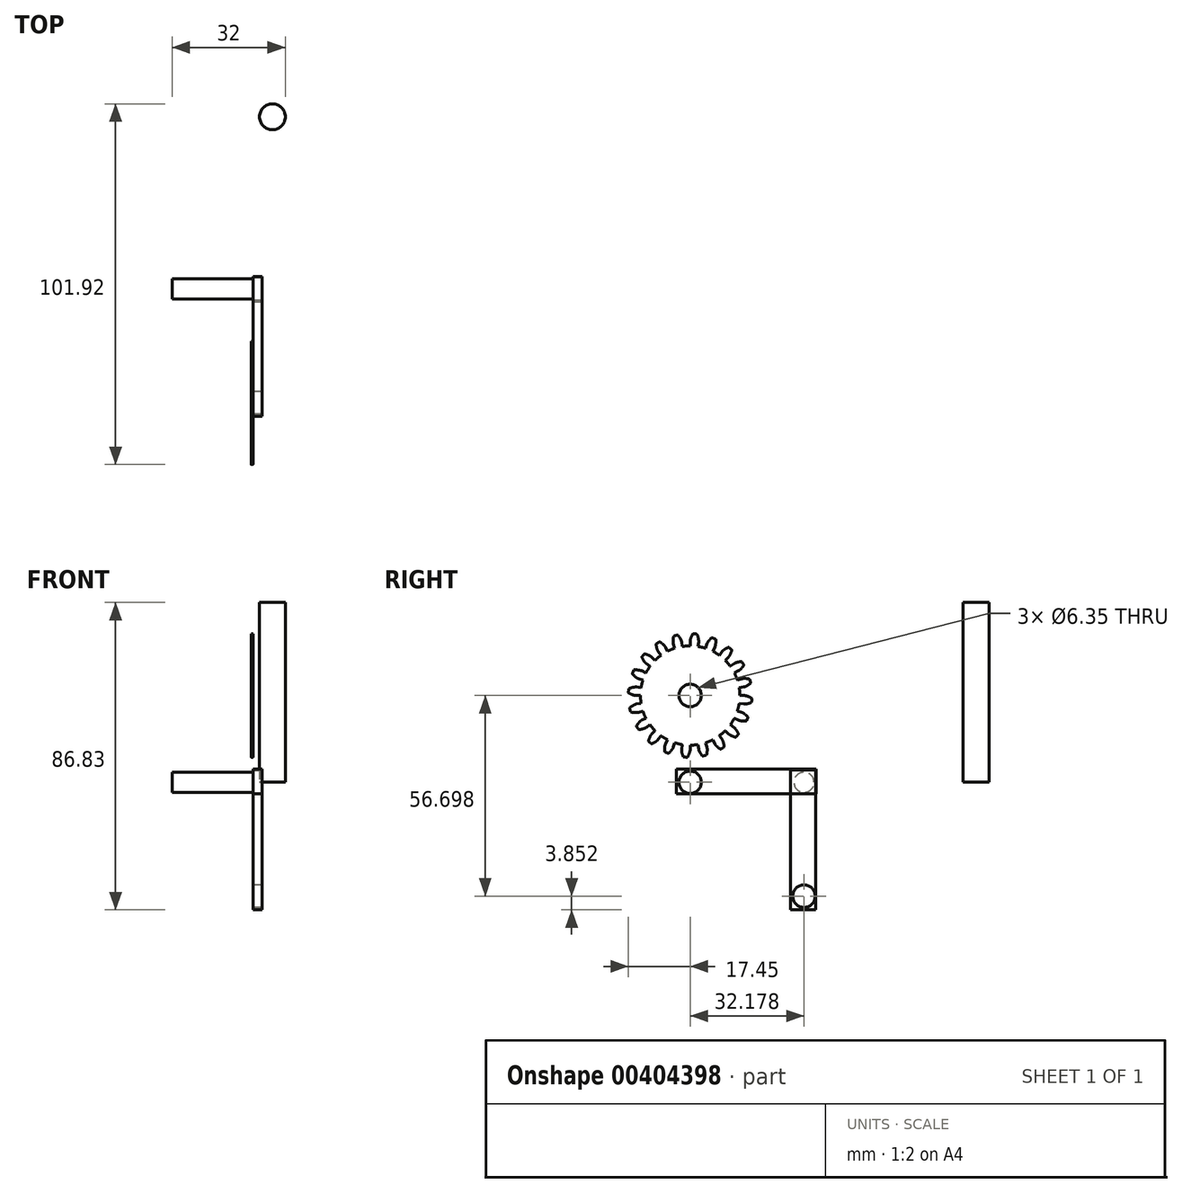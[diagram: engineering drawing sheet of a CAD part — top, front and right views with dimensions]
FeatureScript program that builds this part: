
annotation { "Feature Type Name" : "Feature", "Feature Type Description" : "" }
export const myFeature = defineFeature(function(context is Context, id is Id, definition is map)
    precondition{}
    {
        {
            assignVariable(context, id + "F0", {"name" : "NumberTeeth", "anyValue" : 20});
        }
        {
            assignVariable(context, id + "F1", {"name" : "GearThickness", "anyValue" : .5});
        }
        {
            var Q0;
            Q0=qCreatedBy(makeId("Right.planeOp"),FACE);
            var sketch = newSketch(context, id + "F2", { "sketchPlane" : qUnion([Q0])});
            skCircle(sketch, "E0", {"center": v(0, 0) * mm, "radius": 14.04 * mm});
            skCircle(sketch, "E1", {"center": v(0, 0) * mm, "radius": 15.37 * mm, "construction": true});
            skCircle(sketch, "E2", {"center": v(0, 0) * mm, "radius": 15.88 * mm, "construction": true});
            skCircle(sketch, "E3", {"center": v(0, 0) * mm, "radius": 17.46 * mm});
            skLineSegment(sketch, "E4", {"start": v(0, 0) * mm, "end": v(-15.37, 0) * mm, "construction": true});
            skLineSegment(sketch, "E5.1.0", {"start": v(0, 0) * mm, "end": v(-15.35, 0.77) * mm, "construction": true});
            skLineSegment(sketch, "E5.2.0", {"start": v(0, 0) * mm, "end": v(-15.3, 1.53) * mm, "construction": true});
            skLineSegment(sketch, "E5.3.0", {"start": v(0, 0) * mm, "end": v(-15.2, 2.3) * mm, "construction": true});
            skLineSegment(sketch, "E5.4.0", {"start": v(0, 0) * mm, "end": v(-15.06, 3.05) * mm, "construction": true});
            skLineSegment(sketch, "E5.5.0", {"start": v(0, 0) * mm, "end": v(-14.9, 3.8) * mm, "construction": true});
            skLineSegment(sketch, "E5.6.0", {"start": v(0, 0) * mm, "end": v(-14.68, 4.54) * mm, "construction": true});
            skLineSegment(sketch, "E5.7.0", {"start": v(0, 0) * mm, "end": v(-14.44, 5.27) * mm, "construction": true});
            skLineSegment(sketch, "E5.8.0", {"start": v(0, 0) * mm, "end": v(-14.16, 5.99) * mm, "construction": true});
            skLineSegment(sketch, "E5.9.0", {"start": v(0, 0) * mm, "end": v(-13.84, 6.69) * mm, "construction": true});
            skLineSegment(sketch, "E5.10.0", {"start": v(0, 0) * mm, "end": v(-13.49, 7.37) * mm, "construction": true});
            skLineSegment(sketch, "E5.11.0", {"start": v(0, 0) * mm, "end": v(-13.1, 8.03) * mm, "construction": true});
            skLineSegment(sketch, "E5.12.0", {"start": v(0, 0) * mm, "end": v(-12.68, 8.68) * mm, "construction": true});
            skLineSegment(sketch, "E5.13.0", {"start": v(0, 0) * mm, "end": v(-12.24, 9.3) * mm, "construction": true});
            skLineSegment(sketch, "E5.14.0", {"start": v(0, 0) * mm, "end": v(-11.76, 9.9) * mm, "construction": true});
            skLineSegment(sketch, "E5.anchor2", {"start": v(0, 0) * mm, "end": v(-11.76, 9.9) * mm, "construction": true});
            skLineSegment(sketch, "E6", {"start": v(-15.35, 0.77) * mm, "end": v(-15.39, 0) * mm, "construction": true});
            skLineSegment(sketch, "E7", {"start": v(-15.3, 1.53) * mm, "end": v(-15.45, 0) * mm, "construction": true});
            skLineSegment(sketch, "E8", {"start": v(-15.2, 2.3) * mm, "end": v(-15.54, 0.02) * mm, "construction": true});
            skLineSegment(sketch, "E9", {"start": v(-14.9, 3.8) * mm, "end": v(-15.84, 0.08) * mm, "construction": true});
            skLineSegment(sketch, "E10", {"start": v(-14.68, 4.54) * mm, "end": v(-16.05, 0.14) * mm, "construction": true});
            skLineSegment(sketch, "E11", {"start": v(-14.44, 5.27) * mm, "end": v(-16.28, 0.22) * mm, "construction": true});
            skLineSegment(sketch, "E12", {"start": v(-14.16, 5.99) * mm, "end": v(-16.55, 0.32) * mm, "construction": true});
            skLineSegment(sketch, "E13", {"start": v(-13.84, 6.69) * mm, "end": v(-16.85, 0.46) * mm, "construction": true});
            skLineSegment(sketch, "E14", {"start": v(-13.49, 7.37) * mm, "end": v(-17.17, 0.62) * mm, "construction": true});
            skLineSegment(sketch, "E15", {"start": v(-13.1, 8.03) * mm, "end": v(-17.52, 0.83) * mm, "construction": true});
            skLineSegment(sketch, "E16", {"start": v(-15.06, 3.05) * mm, "end": v(-15.67, 0.04) * mm, "construction": true});
            skLineSegment(sketch, "E17", {"start": v(-12.68, 8.68) * mm, "end": v(-17.9, 1.07) * mm, "construction": true});
            skLineSegment(sketch, "E18", {"start": v(-12.24, 9.3) * mm, "end": v(-18.28, 1.35) * mm, "construction": true});
            skLineSegment(sketch, "E19", {"start": v(-11.76, 9.9) * mm, "end": v(-18.69, 1.67) * mm, "construction": true});
            skLineSegment(sketch, "E20", {"start": v(0, 0) * mm, "end": v(-15.32, 1.2) * mm, "construction": true});
            skLineSegment(sketch, "E21", {"start": v(-14.04, 0) * mm, "end": v(-15.37, 0) * mm});
            skLineSegment(sketch, "E22.MirrorCS", {"start": v(-13.87, 2.2) * mm, "end": v(-15.18, 2.4) * mm});
            skFitSpline(sketch, "E23", {"points": [v(-15.37, 0) * mm, v(-15.39, 0) * mm, v(-15.45, 0) * mm, v(-15.54, 0.02) * mm, v(-15.67, 0.04) * mm, v(-15.84, 0.08) * mm, v(-16.05, 0.14) * mm, v(-16.28, 0.22) * mm, v(-16.55, 0.32) * mm, v(-16.85, 0.46) * mm, v(-17.17, 0.62) * mm, v(-17.52, 0.83) * mm, v(-17.9, 1.07) * mm, v(-18.28, 1.35) * mm, v(-18.69, 1.67) * mm], "startDerivative": vector(-0.82, 0) * mm, "endDerivative": vector(-1.2, 1) * mm});
            skLineSegment(sketch, "E24", {"start": v(-18.69, 1.67) * mm, "end": v(-19.04, 1.97) * mm, "construction": true});
            skFitSpline(sketch, "E25.MirrorCS", {"points": [v(-15.18, 2.4) * mm, v(-15.2, 2.4) * mm, v(-15.26, 2.41) * mm, v(-15.35, 2.41) * mm, v(-15.49, 2.41) * mm, v(-15.66, 2.4) * mm, v(-15.87, 2.37) * mm, v(-16.12, 2.33) * mm, v(-16.4, 2.27) * mm, v(-16.71, 2.18) * mm, v(-17.06, 2.07) * mm, v(-17.43, 1.92) * mm, v(-17.84, 1.74) * mm, v(-18.27, 1.53) * mm, v(-18.72, 1.27) * mm], "startDerivative": vector(-0.8, 0.13) * mm, "endDerivative": vector(-1.34, -0.8) * mm});
            skSolve(sketch);
        }
        {
            var Q0;
            {var subQ0=sQuery(id+"F2.wireOp",EDGE,"E0");var subQ27=makeQuery(id+"F2.imprint","INTERSECT",VERTEX,{"derivedFrom":[subQ0,sQuery(id+"F2.wireOp",EDGE,"10ea1024-8cf5-41f5-a75f-a634b86921f3.10.0")]});Q0=makeQuery(id+"F2.imprint","IMPRINT",FACE,{"disambiguationData":[TD([[makeQuery(id+"F2.imprint","IMPRINT",EDGE,{"disambiguationData":[TD([[subQ27,-1.0]])],"derivedFrom":subQ0}),1.0]])]});}
            var Q1;
            {var subQ0=sQuery(id+"F2.wireOp",EDGE,"10ea1024-8cf5-41f5-a75f-a634b86921f3.1.0");Q1=makeQuery(id+"F2.imprint","IMPRINT",FACE,{"disambiguationData":[TD([[makeQuery(id+"F2.imprint","IMPRINT",EDGE,{"derivedFrom":subQ0}),-1.0]])]});}
            var Q2;
            {var subQ7=sQuery(id+"F2.wireOp",EDGE,"10ea1024-8cf5-41f5-a75f-a634b86921f3.2.0");Q2=makeQuery(id+"F2.imprint","IMPRINT",FACE,{"disambiguationData":[TD([[makeQuery(id+"F2.imprint","IMPRINT",EDGE,{"derivedFrom":subQ7}),-1.0]])]});}
            var Q3;
            {var subQ8=sQuery(id+"F2.wireOp",EDGE,"10ea1024-8cf5-41f5-a75f-a634b86921f3.3.0");Q3=makeQuery(id+"F2.imprint","IMPRINT",FACE,{"disambiguationData":[TD([[makeQuery(id+"F2.imprint","IMPRINT",EDGE,{"derivedFrom":subQ8}),-1.0]])]});}
            var Q4;
            {var subQ2=sQuery(id+"F2.wireOp",EDGE,"10ea1024-8cf5-41f5-a75f-a634b86921f3.4.0");Q4=makeQuery(id+"F2.imprint","IMPRINT",FACE,{"disambiguationData":[TD([[makeQuery(id+"F2.imprint","IMPRINT",EDGE,{"derivedFrom":subQ2}),-1.0]])]});}
            var Q5;
            {var subQ8=sQuery(id+"F2.wireOp",EDGE,"10ea1024-8cf5-41f5-a75f-a634b86921f3.5.0");Q5=makeQuery(id+"F2.imprint","IMPRINT",FACE,{"disambiguationData":[TD([[makeQuery(id+"F2.imprint","IMPRINT",EDGE,{"derivedFrom":subQ8}),-1.0]])]});}
            var Q6;
            {var subQ3=sQuery(id+"F2.wireOp",EDGE,"10ea1024-8cf5-41f5-a75f-a634b86921f3.6.0");Q6=makeQuery(id+"F2.imprint","IMPRINT",FACE,{"disambiguationData":[TD([[makeQuery(id+"F2.imprint","IMPRINT",EDGE,{"derivedFrom":subQ3}),-1.0]])]});}
            var Q7;
            {var subQ0=sQuery(id+"F2.wireOp",EDGE,"10ea1024-8cf5-41f5-a75f-a634b86921f3.7.0");Q7=makeQuery(id+"F2.imprint","IMPRINT",FACE,{"disambiguationData":[TD([[makeQuery(id+"F2.imprint","IMPRINT",EDGE,{"derivedFrom":subQ0}),-1.0]])]});}
            var Q8;
            {var subQ5=sQuery(id+"F2.wireOp",EDGE,"10ea1024-8cf5-41f5-a75f-a634b86921f3.8.0");Q8=makeQuery(id+"F2.imprint","IMPRINT",FACE,{"disambiguationData":[TD([[makeQuery(id+"F2.imprint","IMPRINT",EDGE,{"derivedFrom":subQ5}),-1.0]])]});}
            var Q9;
            {var subQ1=sQuery(id+"F2.wireOp",EDGE,"10ea1024-8cf5-41f5-a75f-a634b86921f3.9.0");Q9=makeQuery(id+"F2.imprint","IMPRINT",FACE,{"disambiguationData":[TD([[makeQuery(id+"F2.imprint","IMPRINT",EDGE,{"derivedFrom":subQ1}),-1.0]])]});}
            var Q10;
            {var subQ5=sQuery(id+"F2.wireOp",EDGE,"10ea1024-8cf5-41f5-a75f-a634b86921f3.10.0");Q10=makeQuery(id+"F2.imprint","IMPRINT",FACE,{"disambiguationData":[TD([[makeQuery(id+"F2.imprint","IMPRINT",EDGE,{"derivedFrom":subQ5}),-1.0]])]});}
            var Q11;
            {var subQ8=sQuery(id+"F2.wireOp",EDGE,"10ea1024-8cf5-41f5-a75f-a634b86921f3.11.0");Q11=makeQuery(id+"F2.imprint","IMPRINT",FACE,{"disambiguationData":[TD([[makeQuery(id+"F2.imprint","IMPRINT",EDGE,{"derivedFrom":subQ8}),-1.0]])]});}
            var Q12;
            {var subQ2=sQuery(id+"F2.wireOp",EDGE,"10ea1024-8cf5-41f5-a75f-a634b86921f3.12.0");Q12=makeQuery(id+"F2.imprint","IMPRINT",FACE,{"disambiguationData":[TD([[makeQuery(id+"F2.imprint","IMPRINT",EDGE,{"derivedFrom":subQ2}),-1.0]])]});}
            var Q13;
            {var subQ3=sQuery(id+"F2.wireOp",EDGE,"10ea1024-8cf5-41f5-a75f-a634b86921f3.13.0");Q13=makeQuery(id+"F2.imprint","IMPRINT",FACE,{"disambiguationData":[TD([[makeQuery(id+"F2.imprint","IMPRINT",EDGE,{"derivedFrom":subQ3}),-1.0]])]});}
            var Q14;
            {var subQ0=sQuery(id+"F2.wireOp",EDGE,"10ea1024-8cf5-41f5-a75f-a634b86921f3.14.0");Q14=makeQuery(id+"F2.imprint","IMPRINT",FACE,{"disambiguationData":[TD([[makeQuery(id+"F2.imprint","IMPRINT",EDGE,{"derivedFrom":subQ0}),-1.0]])]});}
            var Q15;
            {var subQ6=sQuery(id+"F2.wireOp",EDGE,"10ea1024-8cf5-41f5-a75f-a634b86921f3.15.0");Q15=makeQuery(id+"F2.imprint","IMPRINT",FACE,{"disambiguationData":[TD([[makeQuery(id+"F2.imprint","IMPRINT",EDGE,{"derivedFrom":subQ6}),-1.0]])]});}
            var Q16;
            {var subQ5=sQuery(id+"F2.wireOp",EDGE,"10ea1024-8cf5-41f5-a75f-a634b86921f3.16.0");Q16=makeQuery(id+"F2.imprint","IMPRINT",FACE,{"disambiguationData":[TD([[makeQuery(id+"F2.imprint","IMPRINT",EDGE,{"derivedFrom":subQ5}),-1.0]])]});}
            var Q17;
            {var subQ7=sQuery(id+"F2.wireOp",EDGE,"10ea1024-8cf5-41f5-a75f-a634b86921f3.17.0");Q17=makeQuery(id+"F2.imprint","IMPRINT",FACE,{"disambiguationData":[TD([[makeQuery(id+"F2.imprint","IMPRINT",EDGE,{"derivedFrom":subQ7}),-1.0]])]});}
            var Q18;
            {var subQ5=sQuery(id+"F2.wireOp",EDGE,"10ea1024-8cf5-41f5-a75f-a634b86921f3.18.0");Q18=makeQuery(id+"F2.imprint","IMPRINT",FACE,{"disambiguationData":[TD([[makeQuery(id+"F2.imprint","IMPRINT",EDGE,{"derivedFrom":subQ5}),-1.0]])]});}
            var Q19;
            {var subQ8=sQuery(id+"F2.wireOp",EDGE,"10ea1024-8cf5-41f5-a75f-a634b86921f3.19.0");Q19=makeQuery(id+"F2.imprint","IMPRINT",FACE,{"disambiguationData":[TD([[makeQuery(id+"F2.imprint","IMPRINT",EDGE,{"derivedFrom":subQ8}),-1.0]])]});}
            var Q20;
            {var subQ8=sQuery(id+"F2.wireOp",EDGE,"E21");Q20=makeQuery(id+"F2.imprint","IMPRINT",FACE,{"disambiguationData":[TD([[makeQuery(id+"F2.imprint","IMPRINT",EDGE,{"derivedFrom":subQ8}),-1.0]])]});}
            extrude(context, id + "F3", {"entities" : qUnion([Q0, Q1, Q2, Q3, Q4, Q5, Q6, Q7, Q8, Q9, Q10, Q11, Q12, Q13, Q14, Q15, Q16, Q17, Q18, Q19, Q20]), "depth" : (getVariable(context, 'GearThickness')) * mm});
        }
        {
            var Q0;
            Q0=makeQuery(id+"F3.opExtrude","SWEPT_FACE",FACE,{"disambiguationData":[OSD([sQuery(id+"F2.wireOp",EDGE,"E25.MirrorCS")])]});
            var Q1;
            Q1=makeQuery(id+"F3.opExtrude","SWEPT_FACE",FACE,{"disambiguationData":[OSD([sQuery(id+"F2.wireOp",EDGE,"E23")])]});
            var Q2;
            Q2=makeQuery(id+"F3.opExtrude","SWEPT_FACE",FACE,{"disambiguationData":[OSD([sQuery(id+"F2.wireOp",EDGE,"E3")])]});
            var Q3;
            Q3=makeQuery(id+"F3.opExtrude","SWEPT_FACE",FACE,{"disambiguationData":[OSD([sQuery(id+"F2.wireOp",EDGE,"E22.MirrorCS")])]});
            var Q4;
            Q4=makeQuery(id+"F3.opExtrude","SWEPT_FACE",FACE,{"disambiguationData":[OSD([sQuery(id+"F2.wireOp",EDGE,"E21")])]});
            var Q5;
            Q5=makeQuery(id+"F3.opExtrude","SWEPT_FACE",FACE,{"disambiguationData":[OSD([sQuery(id+"F2.wireOp",EDGE,"E0")])]});
            circularPattern(context, id + "F4", {"faces" : qUnion([Q0, Q1, Q2, Q3, Q4]), "axis" : qUnion([Q5]), "angle" : 360 * degree, "instanceCount" : getVariable(context, 'NumberTeeth'), "equalSpace" : true, "patternType" : PatternType.FACE});
        }
        {
            var Q0;
            Q0=makeQuery(id+"F3.opExtrude","SWEPT_BODY",BODY,{"disambiguationData":[OSD([sQuery(id+"F2.wireOp",EDGE,"E0"),sQuery(id+"F2.wireOp",EDGE,"E3"),sQuery(id+"F2.wireOp",EDGE,"E21"),sQuery(id+"F2.wireOp",EDGE,"E22.MirrorCS"),sQuery(id+"F2.wireOp",EDGE,"E23"),sQuery(id+"F2.wireOp",EDGE,"E25.MirrorCS")])]});
            transform(context, id + "F5", {"entities" : qUnion([Q0]), "transformType" : TransformType.TRANSLATION_3D, "dx" : 0 * mm, "dy" : 33.33 * mm, "dz" : 0 * mm, "makeCopy" : true});
        }
        {
            var Q0;
            Q0=makeQuery(id+"F5.opPattern","COPY",BODY,{"derivedFrom":makeQuery(id+"F3.opExtrude","SWEPT_BODY",BODY,{"disambiguationData":[OSD([sQuery(id+"F2.wireOp",EDGE,"E0"),sQuery(id+"F2.wireOp",EDGE,"E3"),sQuery(id+"F2.wireOp",EDGE,"E21"),sQuery(id+"F2.wireOp",EDGE,"E22.MirrorCS"),sQuery(id+"F2.wireOp",EDGE,"E23"),sQuery(id+"F2.wireOp",EDGE,"E25.MirrorCS")])]}),"instanceName":"1"});
            transform(context, id + "F6", {"entities" : qUnion([Q0]), "transformType" : TransformType.TRANSLATION_3D, "dx" : 0 * mm, "dy" : -1.59 * mm, "dz" : 0 * mm, "makeCopy" : false});
        }
        {
            var Q0;
            Q0=makeQuery(id+"F3.opExtrude","CAP_FACE",FACE,{"disambiguationData":[OSD([sQuery(id+"F2.wireOp",EDGE,"E0"),sQuery(id+"F2.wireOp",EDGE,"E3"),sQuery(id+"F2.wireOp",EDGE,"E21"),sQuery(id+"F2.wireOp",EDGE,"E22.MirrorCS"),sQuery(id+"F2.wireOp",EDGE,"E23"),sQuery(id+"F2.wireOp",EDGE,"E25.MirrorCS")])],"isStart":false});
            var sketch = newSketch(context, id + "F7", { "sketchPlane" : qUnion([Q0])});
            skPoint(sketch, "E26", {"position": v(0, 0) * mm});
            skPoint(sketch, "E27", {"position": v(32.12, 0) * mm});
            skSolve(sketch);
        }
        {
            var Q0;
            Q0=sQuery(id+"F7.wireOp",VERTEX,"E26");
            var Q1;
            Q1=sQuery(id+"F7.wireOp",VERTEX,"E27");
            var Q2;
            Q2=makeQuery(id+"F3.opExtrude","SWEPT_BODY",BODY,{"disambiguationData":[OSD([sQuery(id+"F2.wireOp",EDGE,"E0"),sQuery(id+"F2.wireOp",EDGE,"E3"),sQuery(id+"F2.wireOp",EDGE,"E21"),sQuery(id+"F2.wireOp",EDGE,"E22.MirrorCS"),sQuery(id+"F2.wireOp",EDGE,"E23"),sQuery(id+"F2.wireOp",EDGE,"E25.MirrorCS")])]});
            var Q3;
            Q3=makeQuery(id+"F5.opPattern","COPY",BODY,{"derivedFrom":makeQuery(id+"F3.opExtrude","SWEPT_BODY",BODY,{"disambiguationData":[OSD([sQuery(id+"F2.wireOp",EDGE,"E0"),sQuery(id+"F2.wireOp",EDGE,"E3"),sQuery(id+"F2.wireOp",EDGE,"E21"),sQuery(id+"F2.wireOp",EDGE,"E22.MirrorCS"),sQuery(id+"F2.wireOp",EDGE,"E23"),sQuery(id+"F2.wireOp",EDGE,"E25.MirrorCS")])]}),"instanceName":"1"});
            hole(context, id + "F8", {"style" : HoleStyle.SIMPLE, "endStyle" : HoleEndStyle.THROUGH, "holeDiameter" : 6.35 * mm, "majorDiameter" : 6.35 * mm, "isTappedThrough" : true, "tappedDepth" : 12.7 * mm, "tapClearance" : 3, "locations" : qUnion([Q0, Q1]), "scope" : qUnion([Q2, Q3])});
        }
        {
            var Q0;
            Q0=makeQuery(id+"F3.opExtrude","CAP_FACE",FACE,{"disambiguationData":[OSD([sQuery(id+"F2.wireOp",EDGE,"E0"),sQuery(id+"F2.wireOp",EDGE,"E3"),sQuery(id+"F2.wireOp",EDGE,"E21"),sQuery(id+"F2.wireOp",EDGE,"E22.MirrorCS"),sQuery(id+"F2.wireOp",EDGE,"E23"),sQuery(id+"F2.wireOp",EDGE,"E25.MirrorCS")])],"isStart":false});
            var sketch = newSketch(context, id + "F9", { "sketchPlane" : qUnion([Q0])});
            skCircle(sketch, "E28", {"center": v(0, 0) * mm, "radius": 2.7 * mm});
            skCircle(sketch, "E29", {"center": v(32.18, 0) * mm, "radius": 2.84 * mm});
            skPoint(sketch, "E30.oppositeSnap0", {"position": v(13.65, -3.28) * mm});
            skLineSegment(sketch, "E30.bottom", {"start": v(-3.85, 3.78) * mm, "end": v(35.66, 3.78) * mm});
            skLineSegment(sketch, "E30.top", {"start": v(-3.85, -3.28) * mm, "end": v(35.66, -3.28) * mm});
            skLineSegment(sketch, "E30.left", {"start": v(-3.85, 3.78) * mm, "end": v(-3.85, -3.28) * mm});
            skLineSegment(sketch, "E30.right", {"start": v(35.66, 3.78) * mm, "end": v(35.66, -3.28) * mm});
            skSolve(sketch);
        }
        {
            var Q0;
            Q0=makeQuery(id+"F3.opExtrude","SWEPT_BODY",BODY,{"disambiguationData":[OSD([sQuery(id+"F2.wireOp",EDGE,"E0"),sQuery(id+"F2.wireOp",EDGE,"E3"),sQuery(id+"F2.wireOp",EDGE,"E21"),sQuery(id+"F2.wireOp",EDGE,"E22.MirrorCS"),sQuery(id+"F2.wireOp",EDGE,"E23"),sQuery(id+"F2.wireOp",EDGE,"E25.MirrorCS")])]});
            var Q1;
            Q1=makeQuery(id+"F5.opPattern","COPY",BODY,{"derivedFrom":makeQuery(id+"F3.opExtrude","SWEPT_BODY",BODY,{"disambiguationData":[OSD([sQuery(id+"F2.wireOp",EDGE,"E0"),sQuery(id+"F2.wireOp",EDGE,"E3"),sQuery(id+"F2.wireOp",EDGE,"E21"),sQuery(id+"F2.wireOp",EDGE,"E22.MirrorCS"),sQuery(id+"F2.wireOp",EDGE,"E23"),sQuery(id+"F2.wireOp",EDGE,"E25.MirrorCS")])]}),"instanceName":"1"});
            transform(context, id + "F10", {"entities" : qUnion([Q0, Q1]), "transformType" : TransformType.TRANSLATION_3D, "dx" : 0 * mm, "dy" : 0 * mm, "dz" : 24.52 * mm, "makeCopy" : false});
        }
        {
            var Q0;
            Q0=makeQuery(id+"F9.imprint","IMPRINT",FACE,{"disambiguationData":[TD([[makeQuery(id+"F9.imprint","IMPRINT",EDGE,{"derivedFrom":sQuery(id+"F9.wireOp",EDGE,"E29")}),-1.0]])]});
            var Q1;
            {var subQ3=sQuery(id+"F9.wireOp",EDGE,"E30.left");Q1=makeQuery(id+"F9.imprint","IMPRINT",FACE,{"disambiguationData":[TD([[makeQuery(id+"F9.imprint","IMPRINT",EDGE,{"derivedFrom":subQ3}),1.0]])]});}
            extrude(context, id + "F11", {"entities" : qUnion([Q0, Q1]), "depth" : 2.54 * mm, "offsetDistance" : 25.4 * mm});
        }
        {
            var Q0;
            Q0=makeQuery(id+"F11.opExtrude","CAP_FACE",FACE,{"disambiguationData":[OSD([sQuery(id+"F8.hole-0.sketch.wireOp",EDGE,"core_line_2"),sQuery(id+"F8.hole-0.sketch.wireOp",EDGE,"core_line_3"),sQuery(id+"F9.wireOp",EDGE,"E29"),sQuery(id+"F9.wireOp",EDGE,"E30.bottom"),sQuery(id+"F9.wireOp",EDGE,"E30.top"),sQuery(id+"F9.wireOp",EDGE,"E30.left"),sQuery(id+"F9.wireOp",EDGE,"E30.right")])],"isStart":false});
            var sketch = newSketch(context, id + "F12", { "sketchPlane" : qUnion([Q0])});
            skCircle(sketch, "E31", {"center": v(0, 0) * mm, "radius": 3.32 * mm});
            skCircle(sketch, "E32", {"center": v(32.18, 0) * mm, "radius": 2.86 * mm});
            skSolve(sketch);
        }
        {
            var Q0;
            Q0=makeQuery(id+"F12.imprint","IMPRINT",FACE,{"disambiguationData":[TD([[makeQuery(id+"F12.imprint","IMPRINT",EDGE,{"derivedFrom":makeQuery(id+"F11.opExtrude","CAP_EDGE",EDGE,{"disambiguationData":[OSD([sQuery(id+"F8.hole-0.sketch.wireOp",EDGE,"core_line_2"),sQuery(id+"F8.hole-0.sketch.wireOp",EDGE,"core_line_3")])],"isStart":false})}),1.0]])]});
            var Q1;
            Q1=makeQuery(id+"F12.imprint","IMPRINT",FACE,{"disambiguationData":[TD([[makeQuery(id+"F12.imprint","IMPRINT",EDGE,{"derivedFrom":makeQuery(id+"F11.opExtrude","CAP_EDGE",EDGE,{"disambiguationData":[OSD([sQuery(id+"F9.wireOp",EDGE,"E29")])],"isStart":false})}),1.0]])]});
            extrude(context, id + "F13", {"entities" : qUnion([Q0, Q1]), "operationType" : NewBodyOperationType.ADD, "oppositeDirection" : true, "depth" : 25.4 * mm, "offsetDistance" : 25.4 * mm});
        }
        {
            var Q0;
            Q0=makeQuery(id+"F5.opPattern","COPY",BODY,{"derivedFrom":makeQuery(id+"F3.opExtrude","SWEPT_BODY",BODY,{"disambiguationData":[OSD([sQuery(id+"F2.wireOp",EDGE,"E0"),sQuery(id+"F2.wireOp",EDGE,"E3"),sQuery(id+"F2.wireOp",EDGE,"E21"),sQuery(id+"F2.wireOp",EDGE,"E22.MirrorCS"),sQuery(id+"F2.wireOp",EDGE,"E23"),sQuery(id+"F2.wireOp",EDGE,"E25.MirrorCS")])]}),"instanceName":"1"});
            transform(context, id + "F14", {"entities" : qUnion([Q0]), "transformType" : TransformType.TRANSLATION_3D, "dx" : 0 * mm, "dy" : 28.14 * mm, "dz" : 0 * mm, "makeCopy" : false});
        }
        {
            var Q0;
            Q0=qCreatedBy(makeId("Top.planeOp"),FACE);
            var sketch = newSketch(context, id + "F15", { "sketchPlane" : qUnion([Q0])});
            skCircle(sketch, "E33", {"center": v(6, 80.83) * mm, "radius": 3.65 * mm});
            skSolve(sketch);
        }
        {
            var Q0;
            Q0=makeQuery(id+"F15.imprint","IMPRINT",FACE,{"disambiguationData":[TD([[makeQuery(id+"F15.imprint","IMPRINT",EDGE,{"derivedFrom":sQuery(id+"F15.wireOp",EDGE,"E33")}),1.0]])]});
            extrude(context, id + "F16", {"entities" : qUnion([Q0]), "operationType" : NewBodyOperationType.ADD, "depth" : 50.8 * mm, "offsetDistance" : 25.4 * mm});
        }
        {
            var Q0;
            Q0=makeQuery(id+"F5.opPattern","COPY",BODY,{"derivedFrom":makeQuery(id+"F3.opExtrude","SWEPT_BODY",BODY,{"disambiguationData":[OSD([sQuery(id+"F2.wireOp",EDGE,"E0"),sQuery(id+"F2.wireOp",EDGE,"E3"),sQuery(id+"F2.wireOp",EDGE,"E21"),sQuery(id+"F2.wireOp",EDGE,"E22.MirrorCS"),sQuery(id+"F2.wireOp",EDGE,"E23"),sQuery(id+"F2.wireOp",EDGE,"E25.MirrorCS")])]}),"instanceName":"1"});
            deleteBodies(context, id + "F17", {"entities" : qUnion([Q0])});
        }
        {
            var Q0;
            Q0=makeQuery(id+"F11.opExtrude","SWEPT_BODY",BODY,{"disambiguationData":[OSD([sQuery(id+"F8.hole-0.sketch.wireOp",EDGE,"core_line_2"),sQuery(id+"F8.hole-0.sketch.wireOp",EDGE,"core_line_3"),sQuery(id+"F9.wireOp",EDGE,"E29"),sQuery(id+"F9.wireOp",EDGE,"E30.bottom"),sQuery(id+"F9.wireOp",EDGE,"E30.top"),sQuery(id+"F9.wireOp",EDGE,"E30.left"),sQuery(id+"F9.wireOp",EDGE,"E30.right")])]});
            var Q1;
            Q1=makeQuery(id+"F13.opExtrude","SWEPT_FACE",FACE,{"disambiguationData":[OSD([sQuery(id+"F9.wireOp",EDGE,"E29")])]});
            transform(context, id + "F18", {"entities" : qUnion([Q0]), "transformType" : TransformType.ROTATION, "transformAxis" : qUnion([Q1]), "angle" : 90 * degree, "makeCopy" : true});
        }
    });
